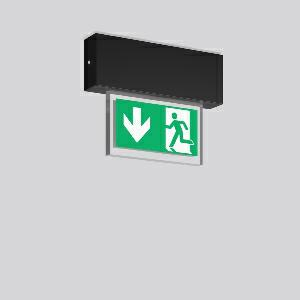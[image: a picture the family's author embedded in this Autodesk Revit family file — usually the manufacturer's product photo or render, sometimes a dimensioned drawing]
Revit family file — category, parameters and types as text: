
# Revit family: halyxx_671502_003_1_04_3c31
name_source: partatom
category: Lighting Fixtures
units: mm (PartAtom-declared; Revit-internal decimal feet)

## family parameters
Cut with Voids When Loaded = No
Host = Face
Light Source = No
Part Type = Normal
Room Calculation Point = No
Round Connector Dimension = Use Diameter
Shared = No

## types (1)
- HALYXX (1 x LED Modul 840, 55 lm, 4000)
    Apparent Load = 3 VA
    Approval mark = CE
    CIE Flux Codes = 18 46 75 53 100
    Color Rendering = 80
    Color Temperature = 4000
    Default Elevation = 1800 mm
    Description = Series: HALYXX
Luminaire for escape route identification. Housing: extruded aluminium profile, anodised or powder-coated. Display panel: highly transparent panel, plastic, with legend on one side/both sides. Electronic ballast included. Self-contained system with automatic self-test and feedback to the RZB monitoring system MULTIDIGIT. Please indicate legend number when placing your order! 
Colour: black
Length: 233 mm
Width: 40 mm
Height: 180 mm
Weight: 1.04 kg
Operating mode: maintained power mode
Viewing Distance: 14 m
Duration time: 3 h
Lamp: LED
Socket: without socket
Colour temperature: 4000K
Colour rendering index (CRI): 80
System power: 3.2 W
Rated luminous flux: 55 lm
Luminous flux, emergency: 30
System power, emergency: -
Control gear: EB
Protection class: I
Type of protection: IP 40
    Height = 180 mm  [stored 0.590551 ft]
    Lamp = 1 x LED Modul 840
    Lamp Light Flux = 55 lm
    Lamp count = 1
    Length = 233 mm
    Lifetime = 50000 h
    Luminous efficacy = 17 lm/W
    Manufacturer = RZB
    ModVariant = No
    Model = 671502.003.1.04
    Mounting Place = Ceiling
    Mounting Type = Surface mounted
    Number of Poles = 1
    OnlyDefault = Yes
    Power Factor = 1
    Product Name = HALYXX
    Product group = Surface mounted ceiling luminaires
    ProductGroupID = 303
    Protection Class = Protection class I
    Protection Degree = IP 40
    RLX_Detail_Level = 1
    RLX_Emergency_Light_Flux = 30 lm
    RLX_Emergency_Type = 3
    RLX_Emergency_Type_DB = Yes
    RlxData = <blob elided: 35021 chars, md5=ec1df584>
    Socket = socket
    Standby Power = 0 W
    System Light Flux = 55 lm
    System Power = 3 W
    Type Comments = Product without accessories
    Type Image = 671502.003.jpg
    URL = http://relux.com
    VarID = ---
    Voltage = 230 V
    Voltage Range = 220-240 V
    Weight = 0.00 kg
    Width = 40 mm  [stored 0.131234 ft]

note: [stored X ft] marks values corroborated as IEEE doubles in the binary element streams (Revit-internal decimal feet)

## geometry (parser evidence)
native form markers: Blend x4, Sweep x12
no freeform markers — native parametric forms only
